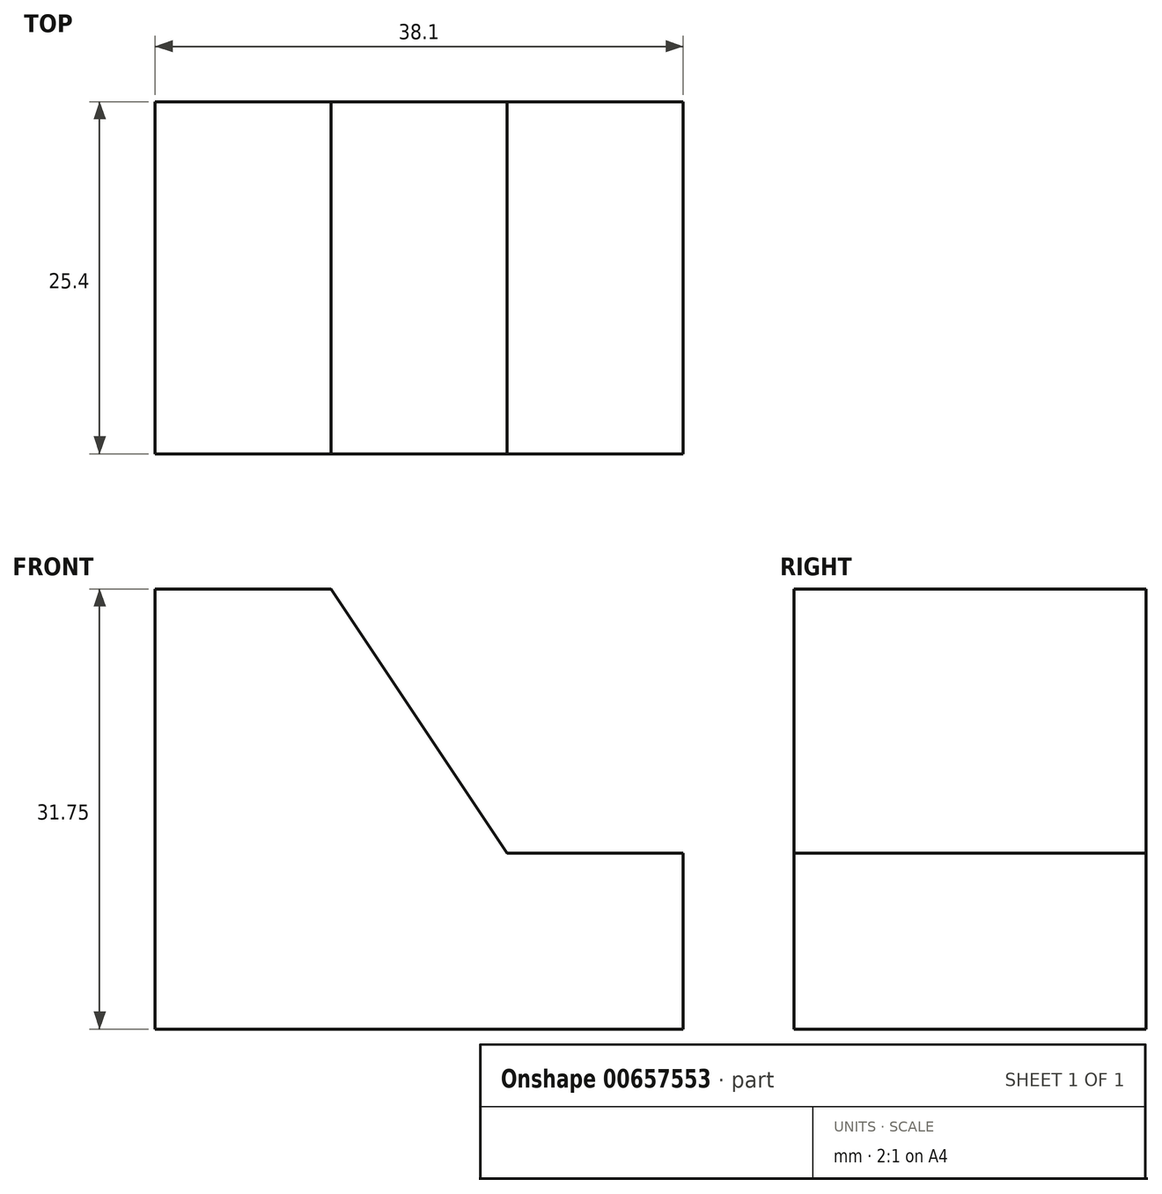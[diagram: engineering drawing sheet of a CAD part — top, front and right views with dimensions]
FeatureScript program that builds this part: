
annotation { "Feature Type Name" : "Feature", "Feature Type Description" : "" }
export const myFeature = defineFeature(function(context is Context, id is Id, definition is map)
    precondition{}
    {
        {
            var Q0;
            Q0=qCreatedBy(makeId("Front.planeOp"),FACE);
            var sketch = newSketch(context, id + "F0", { "sketchPlane" : qUnion([Q0])});
            skLineSegment(sketch, "E0", {"start": v(19.87, 10.07) * mm, "end": v(32.57, 10.07) * mm});
            skLineSegment(sketch, "E1", {"start": v(32.57, 10.07) * mm, "end": v(32.57, -2.63) * mm});
            skLineSegment(sketch, "E2", {"start": v(32.57, -2.63) * mm, "end": v(-5.53, -2.63) * mm});
            skLineSegment(sketch, "E3", {"start": v(-5.53, -2.63) * mm, "end": v(-5.53, 29.12) * mm});
            skLineSegment(sketch, "E4", {"start": v(-5.53, 29.12) * mm, "end": v(7.17, 29.12) * mm});
            skLineSegment(sketch, "E5", {"start": v(7.17, 29.12) * mm, "end": v(19.87, 10.07) * mm});
            skSolve(sketch);
        }
        {
            var Q0;
            Q0=makeQuery(id+"F0.imprint","IMPRINT",FACE,{"disambiguationData":[TD([[makeQuery(id+"F0.imprint","IMPRINT",EDGE,{"derivedFrom":sQuery(id+"F0.wireOp",EDGE,"E0")}),-1.0]])]});
            extrude(context, id + "F1", {"entities" : qUnion([Q0]), "depth" : 25.4 * mm, "offsetDistance" : 25.4 * mm});
        }
    });
